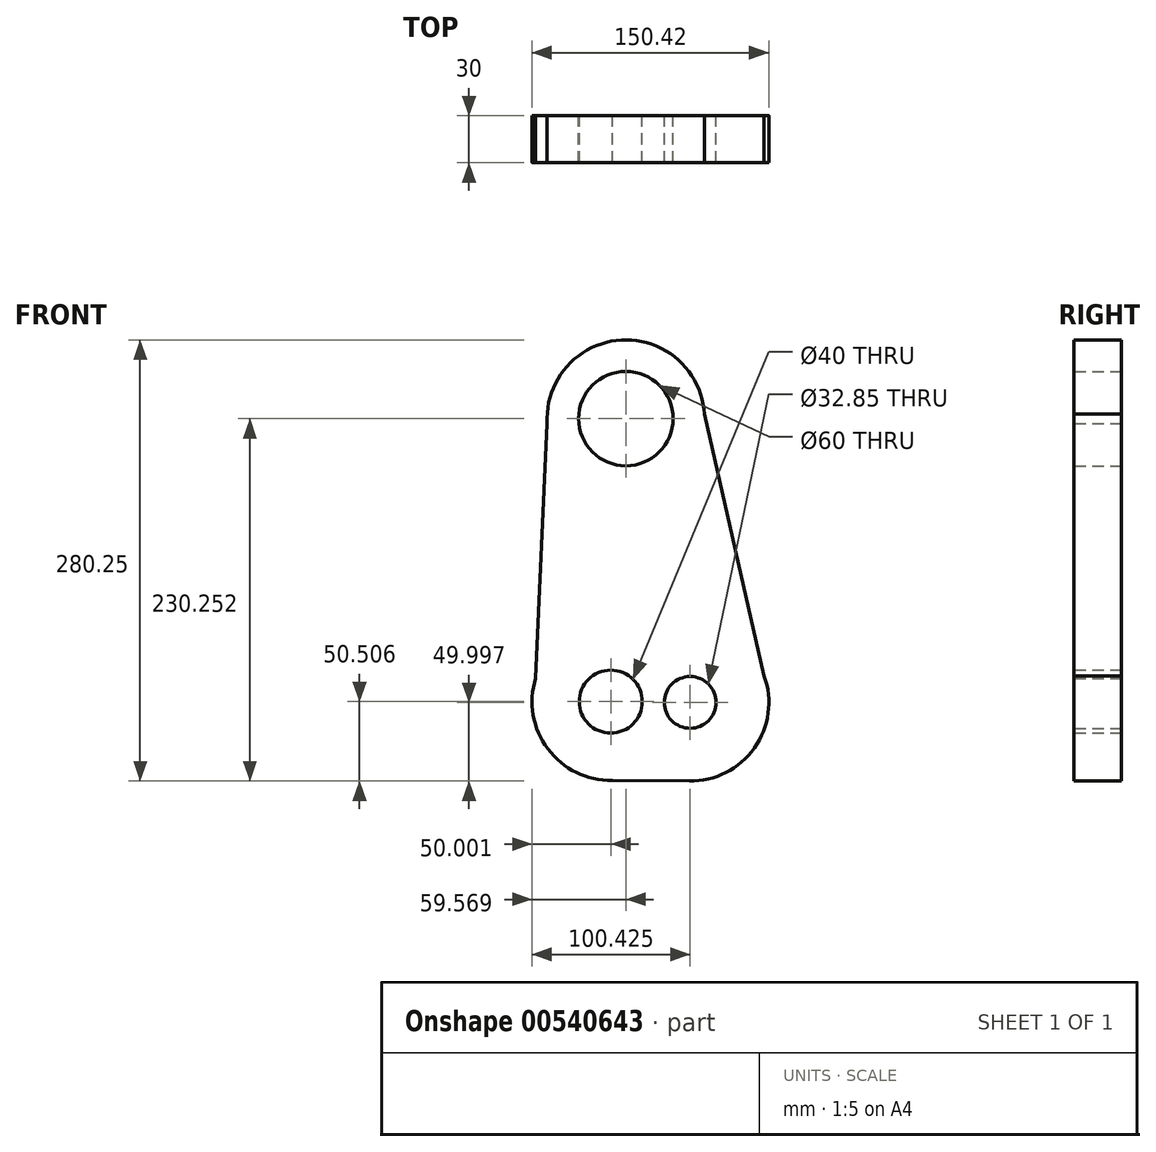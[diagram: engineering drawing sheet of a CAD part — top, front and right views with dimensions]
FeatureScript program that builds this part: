
annotation { "Feature Type Name" : "Feature", "Feature Type Description" : "" }
export const myFeature = defineFeature(function(context is Context, id is Id, definition is map)
    precondition{}
    {
        {
            var Q0;
            Q0=qCreatedBy(makeId("Front.planeOp"),FACE);
            var sketch = newSketch(context, id + "F0", { "sketchPlane" : qUnion([Q0])});
            skCircle(sketch, "E0", {"center": v(-34.04, -80.2) * mm, "radius": 10 * mm});
            skCircle(sketch, "E1", {"center": v(-34.04, -80.2) * mm, "radius": 20 * mm});
            skCircle(sketch, "E2", {"center": v(16.38, -80.7) * mm, "radius": 16.43 * mm});
            skPoint(sketch, "E3.end.orphan", {"position": v(0, 140.14) * mm});
            skCircle(sketch, "E4", {"center": v(-24.47, 99.55) * mm, "radius": 16 * mm});
            skCircle(sketch, "E5", {"center": v(-24.47, 99.55) * mm, "radius": 30 * mm});
            skCircle(sketch, "E6", {"center": v(-24.47, 99.55) * mm, "radius": 50 * mm});
            skArc(sketch, "E7", {"start": v(-8.4, -37.27) * mm, "mid": v(-84.04, -79.69) * mm, "end": v(-9.26, -123.62) * mm});
            skLineSegment(sketch, "E8", {"start": v(-36.05, -130.15) * mm, "end": v(15.86, -130.7) * mm});
            skLineSegment(sketch, "E9", {"start": v(21.7, 118.75) * mm, "end": v(66.12, -75.53) * mm});
            skLineSegment(sketch, "E10", {"start": v(-73.9, 107.05) * mm, "end": v(-82.95, -90.55) * mm});
            skArc(sketch, "E11.trimOffspring", {"start": v(-9.26, -123.62) * mm, "mid": v(66.38, -81.2) * mm, "end": v(-8.4, -37.27) * mm});
            skSolve(sketch);
        }
        {
            var Q0;
            Q0 = qSketchRegion(id + "F0", true);
            extrude(context, id + "F1", {"entities" : qUnion([Q0]), "depth" : 30 * mm, "offsetDistance" : 25 * mm});
        }
    });
